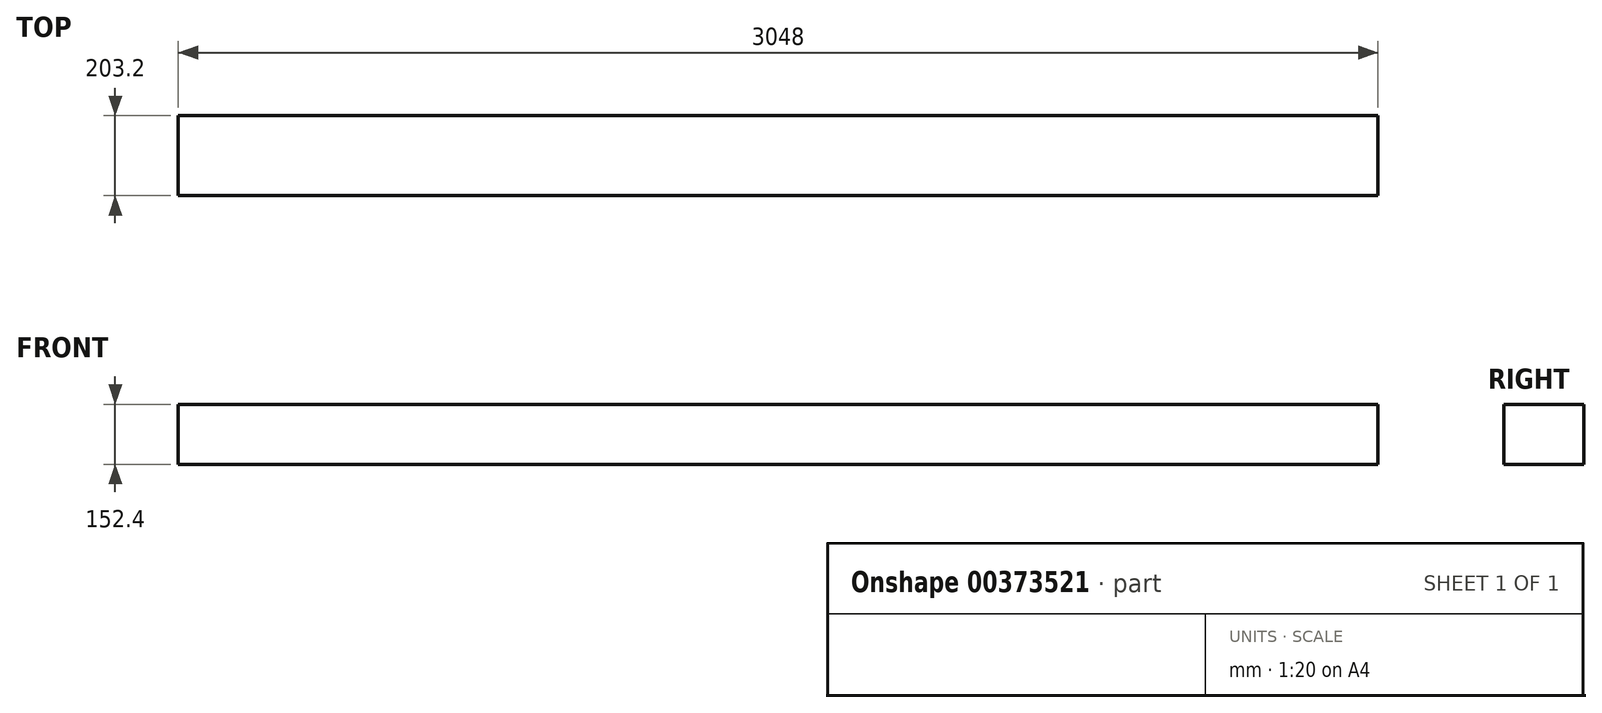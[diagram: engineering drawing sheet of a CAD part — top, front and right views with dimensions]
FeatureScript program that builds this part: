
annotation { "Feature Type Name" : "Feature", "Feature Type Description" : "" }
export const myFeature = defineFeature(function(context is Context, id is Id, definition is map)
    precondition{}
    {
        {
            var Q0;
            Q0=qCreatedBy(makeId("Top.planeOp"),FACE);
            var sketch = newSketch(context, id + "F0", { "sketchPlane" : qUnion([Q0])});
            skLineSegment(sketch, "E0.bottom", {"start": v(-424.08, 97.53) * mm, "end": v(2623.92, 97.53) * mm});
            skLineSegment(sketch, "E0.top", {"start": v(-424.08, -105.67) * mm, "end": v(2623.92, -105.67) * mm});
            skLineSegment(sketch, "E0.left", {"start": v(-424.08, 97.53) * mm, "end": v(-424.08, -105.67) * mm});
            skLineSegment(sketch, "E0.right", {"start": v(2623.92, 97.53) * mm, "end": v(2623.92, -105.67) * mm});
            skSolve(sketch);
        }
        {
            var Q0;
            Q0 = qSketchRegion(id + "F0", true);
            extrude(context, id + "F1", {"entities" : qUnion([Q0]), "depth" : 152.4 * mm});
        }
    });
